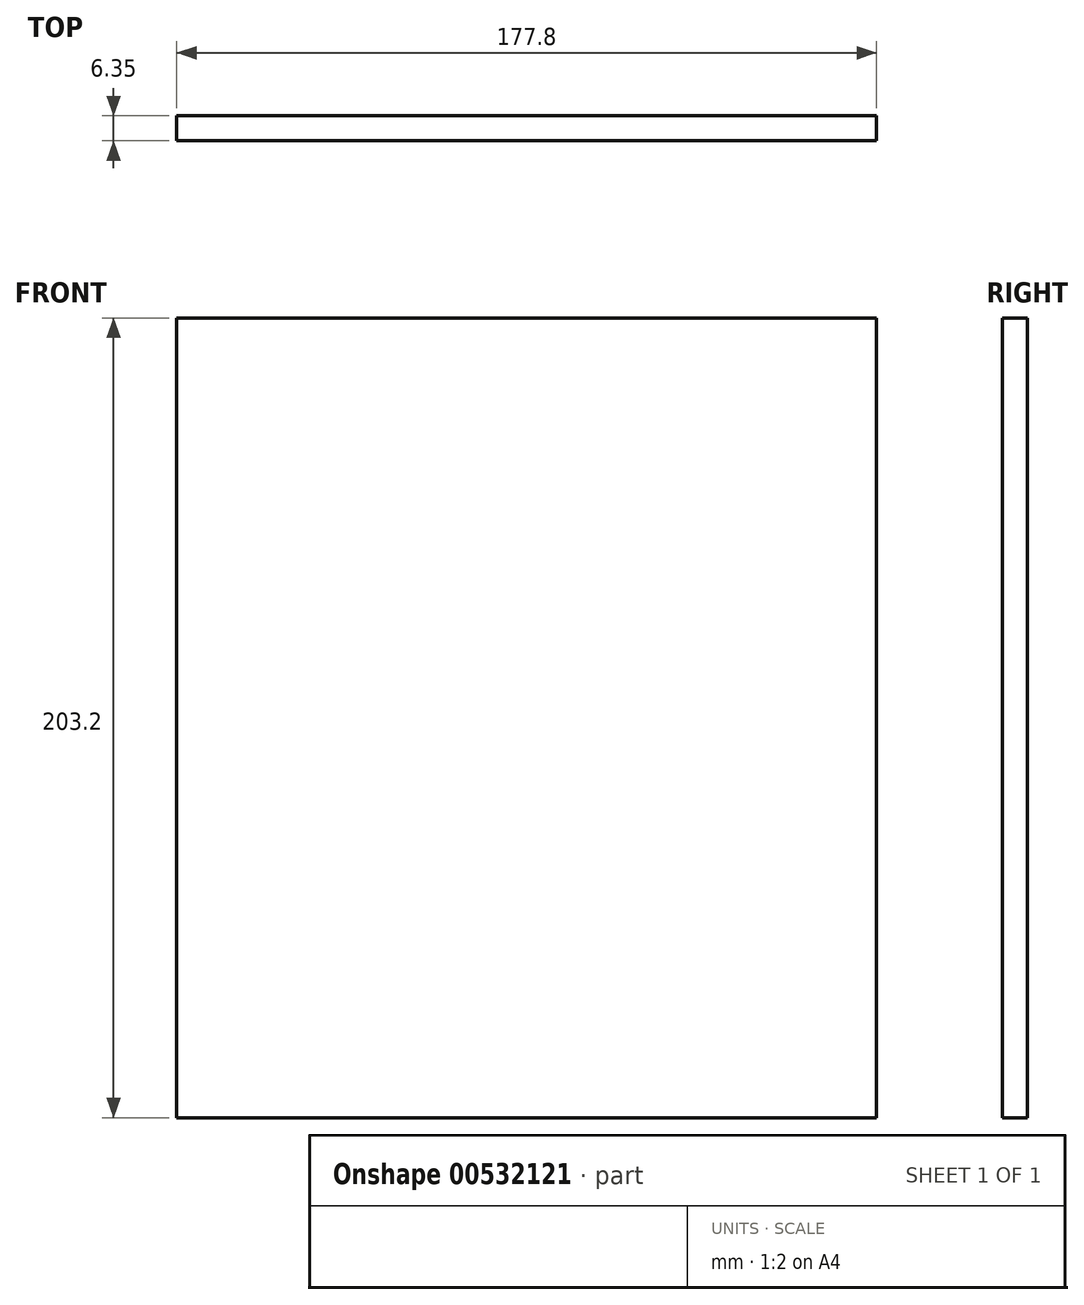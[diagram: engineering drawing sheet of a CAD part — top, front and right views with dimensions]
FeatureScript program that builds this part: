
annotation { "Feature Type Name" : "Feature", "Feature Type Description" : "" }
export const myFeature = defineFeature(function(context is Context, id is Id, definition is map)
    precondition{}
    {
        {
            var Q0;
            Q0=qCreatedBy(makeId("Front.planeOp"),FACE);
            var sketch = newSketch(context, id + "F0", { "sketchPlane" : qUnion([Q0])});
            skLineSegment(sketch, "E0.bottom", {"start": v(88.9, -101.6) * mm, "end": v(-88.9, -101.6) * mm});
            skLineSegment(sketch, "E0.top", {"start": v(88.9, 101.6) * mm, "end": v(-88.9, 101.6) * mm});
            skLineSegment(sketch, "E0.left", {"start": v(88.9, -101.6) * mm, "end": v(88.9, 101.6) * mm});
            skLineSegment(sketch, "E0.right", {"start": v(-88.9, -101.6) * mm, "end": v(-88.9, 101.6) * mm});
            skPoint(sketch, "E0.middle", {"position": v(0, 0) * mm});
            skSolve(sketch);
        }
        {
            var Q0;
            Q0 = qSketchRegion(id + "F0", true);
            extrude(context, id + "F1", {"entities" : qUnion([Q0]), "depth" : 6.35 * mm, "offsetDistance" : 25.4 * mm});
        }
    });
